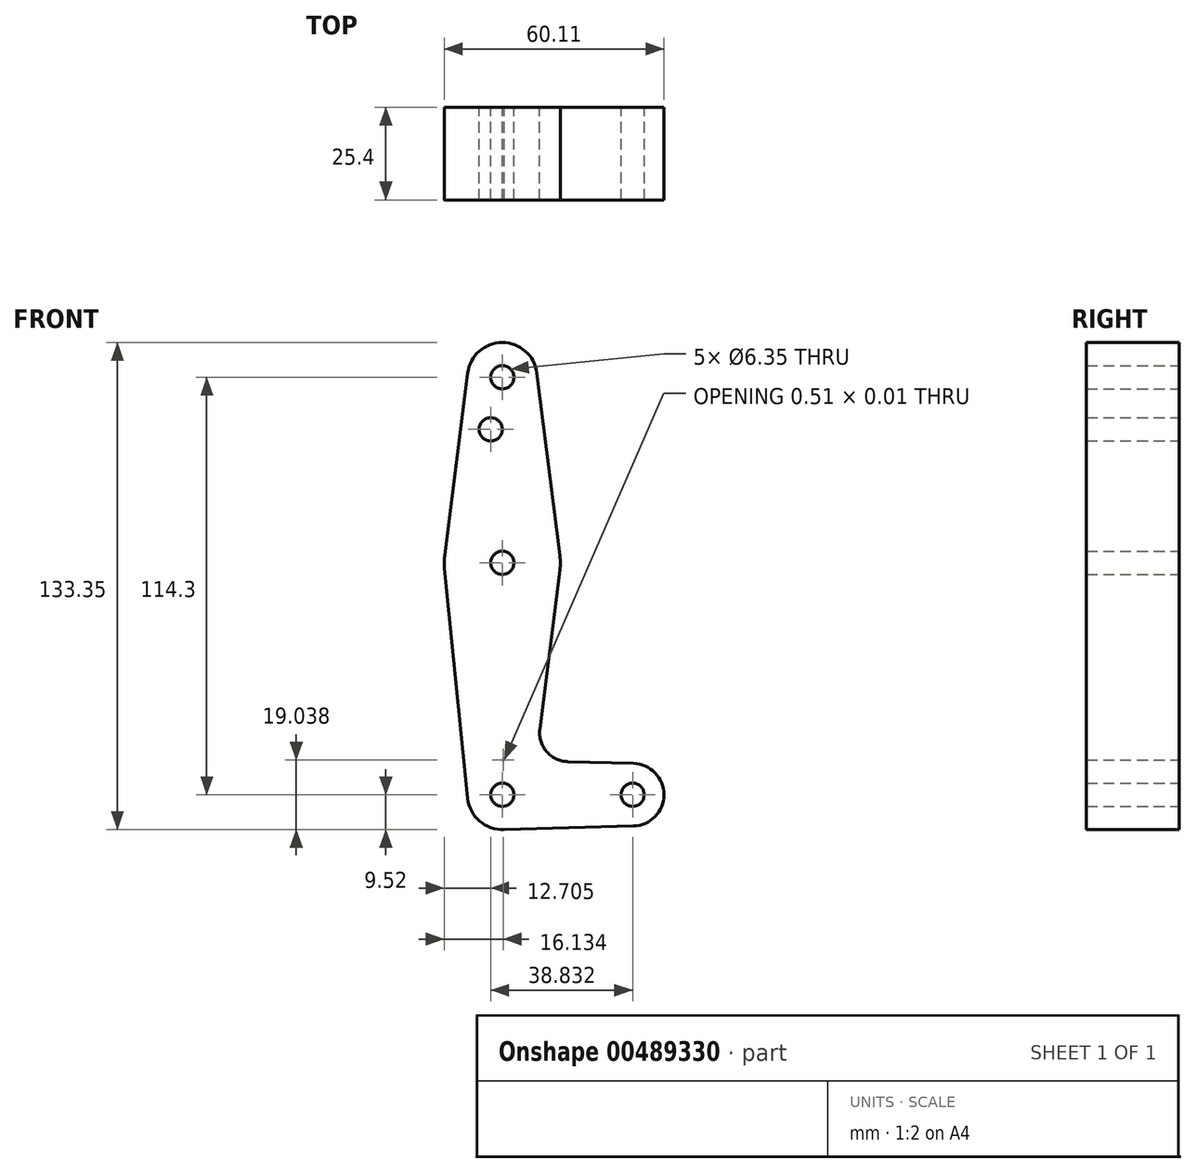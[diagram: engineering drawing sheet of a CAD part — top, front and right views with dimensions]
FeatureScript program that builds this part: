
annotation { "Feature Type Name" : "Feature", "Feature Type Description" : "" }
export const myFeature = defineFeature(function(context is Context, id is Id, definition is map)
    precondition{}
    {
        {
            var Q0;
            Q0=qCreatedBy(makeId("Front.planeOp"),FACE);
            var sketch = newSketch(context, id + "F0", { "sketchPlane" : qUnion([Q0])});
            skLineSegment(sketch, "E0", {"start": v(0, 114.3) * mm, "end": v(0, 0) * mm, "construction": true});
            skCircle(sketch, "E1", {"center": v(0, 114.3) * mm, "radius": 9.53 * mm});
            skCircle(sketch, "E2", {"center": v(0, 63.5) * mm, "radius": 15.88 * mm});
            skCircle(sketch, "E3", {"center": v(0, 0) * mm, "radius": 9.53 * mm});
            skPoint(sketch, "E4.center.orphan", {"position": v(30.76, 0) * mm});
            skPoint(sketch, "E5.orphan", {"position": v(35.66, 0) * mm});
            skLineSegment(sketch, "E6", {"start": v(0, 0) * mm, "end": v(35.66, 0) * mm, "construction": true});
            skCircle(sketch, "E7", {"center": v(35.66, 0) * mm, "radius": 8.57 * mm});
            skLineSegment(sketch, "E8", {"start": v(-9.45, 115.5) * mm, "end": v(-15.75, 65.48) * mm});
            skLineSegment(sketch, "E9", {"start": v(9.45, 115.5) * mm, "end": v(15.75, 65.48) * mm});
            skLineSegment(sketch, "E10", {"start": v(15.75, 61.52) * mm, "end": v(10.27, 17.99) * mm});
            skLineSegment(sketch, "E11", {"start": v(0, 9.53) * mm, "end": v(0.5, 9.51) * mm});
            skLineSegment(sketch, "E12", {"start": v(0, -9.53) * mm, "end": v(35.89, -8.57) * mm});
            skCircle(sketch, "E13", {"center": v(0, 114.3) * mm, "radius": 3.18 * mm});
            skCircle(sketch, "E14", {"center": v(0, 63.5) * mm, "radius": 3.18 * mm});
            skCircle(sketch, "E15", {"center": v(0, 0) * mm, "radius": 3.18 * mm});
            skCircle(sketch, "E16", {"center": v(35.66, 0) * mm, "radius": 3.18 * mm});
            skCircle(sketch, "E17", {"center": v(-3.17, 100.03) * mm, "radius": 3.18 * mm});
            skArc(sketch, "E18", {"start": v(10.27, 17.99) * mm, "mid": v(12.12, 11.82) * mm, "end": v(17.94, 9.05) * mm});
            skLineSegment(sketch, "E19.trimOffspring", {"start": v(17.94, 9.05) * mm, "end": v(35.89, 8.57) * mm});
            skPoint(sketch, "E20.end.orphan", {"position": v(-9.57, 0) * mm});
            skLineSegment(sketch, "E21", {"start": v(-9.48, -0.95) * mm, "end": v(-15.8, 61.91) * mm});
            skSolve(sketch);
        }
        {
            var Q0;
            Q0 = qSketchRegion(id + "F0", true);
            extrude(context, id + "F1", {"entities" : qUnion([Q0]), "depth" : 25.4 * mm});
        }
        {
            var Q0;
            Q0 = qSketchRegion(id + "F0", true);
            extrude(context, id + "F2", {"entities" : qUnion([Q0]), "operationType" : NewBodyOperationType.ADD, "depth" : 25.4 * mm});
        }
    });
